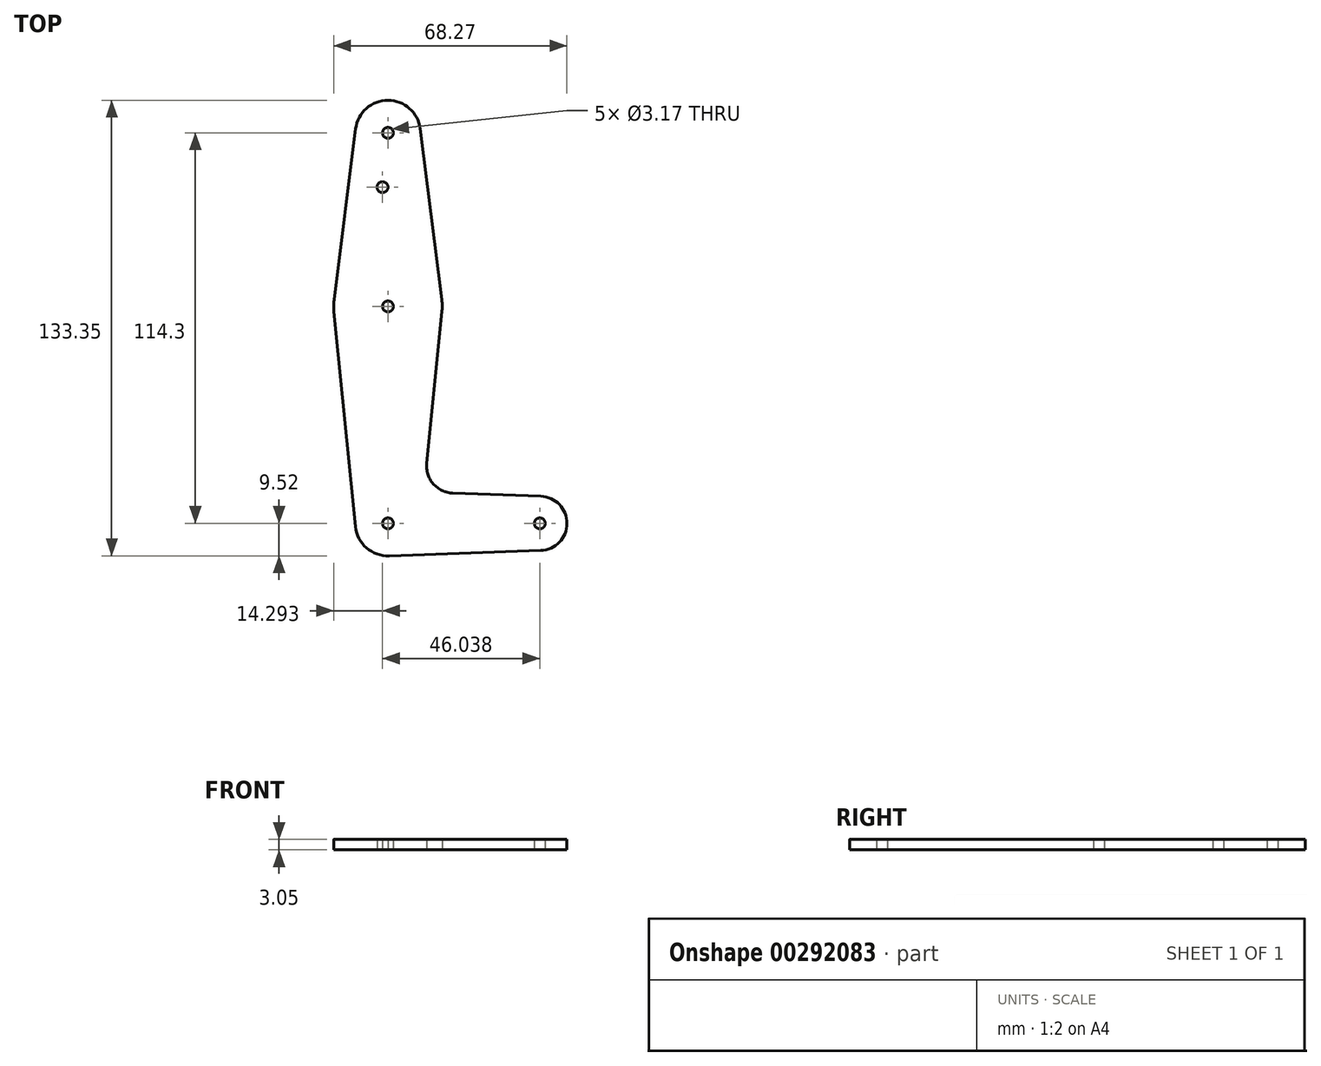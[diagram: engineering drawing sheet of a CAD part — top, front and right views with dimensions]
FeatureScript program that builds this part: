
annotation { "Feature Type Name" : "Feature", "Feature Type Description" : "" }
export const myFeature = defineFeature(function(context is Context, id is Id, definition is map)
    precondition{}
    {
        {
            var Q0;
            Q0=qCreatedBy(makeId("Top.planeOp"),FACE);
            var sketch = newSketch(context, id + "F0", { "sketchPlane" : qUnion([Q0])});
            skLineSegment(sketch, "E0", {"start": v(0, 0) * mm, "end": v(0, 114.3) * mm});
            skCircle(sketch, "E1", {"center": v(0, 114.3) * mm, "radius": 9.53 * mm});
            skCircle(sketch, "E2", {"center": v(0, 63.5) * mm, "radius": 15.88 * mm});
            skCircle(sketch, "E3", {"center": v(0, 0) * mm, "radius": 9.53 * mm});
            skLineSegment(sketch, "E4", {"start": v(0, 0) * mm, "end": v(44.45, 0) * mm});
            skCircle(sketch, "E5", {"center": v(44.45, 0) * mm, "radius": 7.94 * mm});
            skLineSegment(sketch, "E6", {"start": v(9.45, 115.5) * mm, "end": v(15.75, 65.48) * mm});
            skLineSegment(sketch, "E7", {"start": v(15.8, 61.91) * mm, "end": v(11.34, 17.6) * mm});
            skLineSegment(sketch, "E8", {"start": v(-9.45, 115.5) * mm, "end": v(-15.75, 65.48) * mm});
            skLineSegment(sketch, "E9", {"start": v(-15.8, 61.91) * mm, "end": v(-9.48, -0.95) * mm});
            skLineSegment(sketch, "E10", {"start": v(0.34, -9.52) * mm, "end": v(44.73, -7.93) * mm});
            skLineSegment(sketch, "E11", {"start": v(44.73, 7.93) * mm, "end": v(18.97, 8.85) * mm});
            skCircle(sketch, "E12", {"center": v(0, 114.3) * mm, "radius": 1.59 * mm});
            skCircle(sketch, "E13", {"center": v(0, 63.5) * mm, "radius": 1.59 * mm});
            skCircle(sketch, "E14", {"center": v(0, 0) * mm, "radius": 1.59 * mm});
            skCircle(sketch, "E15", {"center": v(44.45, 0) * mm, "radius": 1.59 * mm});
            skCircle(sketch, "E16", {"center": v(-1.59, 98.4) * mm, "radius": 1.59 * mm});
            skArc(sketch, "E17.filletArc", {"start": v(11.34, 17.6) * mm, "mid": v(13.26, 11.57) * mm, "end": v(18.97, 8.85) * mm});
            skSolve(sketch);
        }
        {
            var Q0;
            {var subQ5=sQuery(id+"F0.wireOp",EDGE,"E9");Q0=makeQuery(id+"F0.imprint","IMPRINT",FACE,{"disambiguationData":[TD([[makeQuery(id+"F0.imprint","IMPRINT",EDGE,{"derivedFrom":subQ5}),1.0]])]});}
            var Q1;
            {var subQ0=sQuery(id+"F0.wireOp",EDGE,"E6");Q1=makeQuery(id+"F0.imprint","IMPRINT",FACE,{"disambiguationData":[TD([[makeQuery(id+"F0.imprint","IMPRINT",EDGE,{"derivedFrom":subQ0}),-1.0]])]});}
            var Q2;
            Q2=makeQuery(id+"F0.imprint","IMPRINT",FACE,{"disambiguationData":[TD([[makeQuery(id+"F0.imprint","IMPRINT",EDGE,{"derivedFrom":sQuery(id+"F0.wireOp",EDGE,"E12")}),-1.0]])]});
            var Q3;
            {var subQ0=sQuery(id+"F0.wireOp",EDGE,"E10");Q3=makeQuery(id+"F0.imprint","IMPRINT",FACE,{"disambiguationData":[TD([[makeQuery(id+"F0.imprint","IMPRINT",EDGE,{"derivedFrom":subQ0}),1.0]])]});}
            var Q4;
            Q4=makeQuery(id+"F0.imprint","IMPRINT",FACE,{"disambiguationData":[TD([[makeQuery(id+"F0.imprint","IMPRINT",EDGE,{"derivedFrom":sQuery(id+"F0.wireOp",EDGE,"E15")}),-1.0]])]});
            var Q5;
            {var subQ5=sQuery(id+"F0.wireOp",EDGE,"E0");var subQ7=sQuery(id+"F0.wireOp",EDGE,"E14");var subQ8=makeQuery(id+"F0.imprint","INTERSECT",VERTEX,{"derivedFrom":[subQ5,subQ7]});Q5=makeQuery(id+"F0.imprint","IMPRINT",FACE,{"disambiguationData":[TD([[makeQuery(id+"F0.imprint","IMPRINT",EDGE,{"disambiguationData":[TD([[subQ8,-1.0]])],"derivedFrom":subQ5}),1.0]])]});}
            var Q6;
            {var subQ0=sQuery(id+"F0.wireOp",EDGE,"E2");var subQ2=sQuery(id+"F0.wireOp",EDGE,"E0");var subQ5=makeQuery(id+"F0.imprint","INTERSECT",VERTEX,{"disambiguationData":[OD(0.0)],"derivedFrom":[subQ2,subQ0]});Q6=makeQuery(id+"F0.imprint","IMPRINT",FACE,{"disambiguationData":[TD([[makeQuery(id+"F0.imprint","IMPRINT",EDGE,{"disambiguationData":[TD([[subQ5,-1.0]])],"derivedFrom":subQ2}),-1.0]])]});}
            var Q7;
            {var subQ0=sQuery(id+"F0.wireOp",EDGE,"E2");var subQ2=sQuery(id+"F0.wireOp",EDGE,"E0");var subQ8=makeQuery(id+"F0.imprint","INTERSECT",VERTEX,{"disambiguationData":[OD(0.0)],"derivedFrom":[subQ2,subQ0]});Q7=makeQuery(id+"F0.imprint","IMPRINT",FACE,{"disambiguationData":[TD([[makeQuery(id+"F0.imprint","IMPRINT",EDGE,{"disambiguationData":[TD([[subQ8,-1.0]])],"derivedFrom":subQ2}),1.0]])]});}
            var Q8;
            {var subQ0=sQuery(id+"F0.wireOp",EDGE,"E8");Q8=makeQuery(id+"F0.imprint","IMPRINT",FACE,{"disambiguationData":[TD([[makeQuery(id+"F0.imprint","IMPRINT",EDGE,{"derivedFrom":subQ0}),1.0]])]});}
            var Q9;
            {var subQ5=sQuery(id+"F0.wireOp",EDGE,"E7");Q9=makeQuery(id+"F0.imprint","IMPRINT",FACE,{"disambiguationData":[TD([[makeQuery(id+"F0.imprint","IMPRINT",EDGE,{"derivedFrom":subQ5}),-1.0]])]});}
            var Q10;
            {var subQ0=sQuery(id+"F0.wireOp",EDGE,"E14");var subQ1=sQuery(id+"F0.wireOp",EDGE,"E0");var subQ2=makeQuery(id+"F0.imprint","INTERSECT",VERTEX,{"derivedFrom":[subQ1,subQ0]});Q10=makeQuery(id+"F0.imprint","IMPRINT",FACE,{"disambiguationData":[TD([[makeQuery(id+"F0.imprint","IMPRINT",EDGE,{"disambiguationData":[TD([[subQ2,-1.0]])],"derivedFrom":subQ1}),-1.0]])]});}
            extrude(context, id + "F1", {"entities" : qUnion([Q0, Q1, Q2, Q3, Q4, Q5, Q6, Q7, Q8, Q9, Q10]), "depth" : 3.05 * mm});
        }
    });
